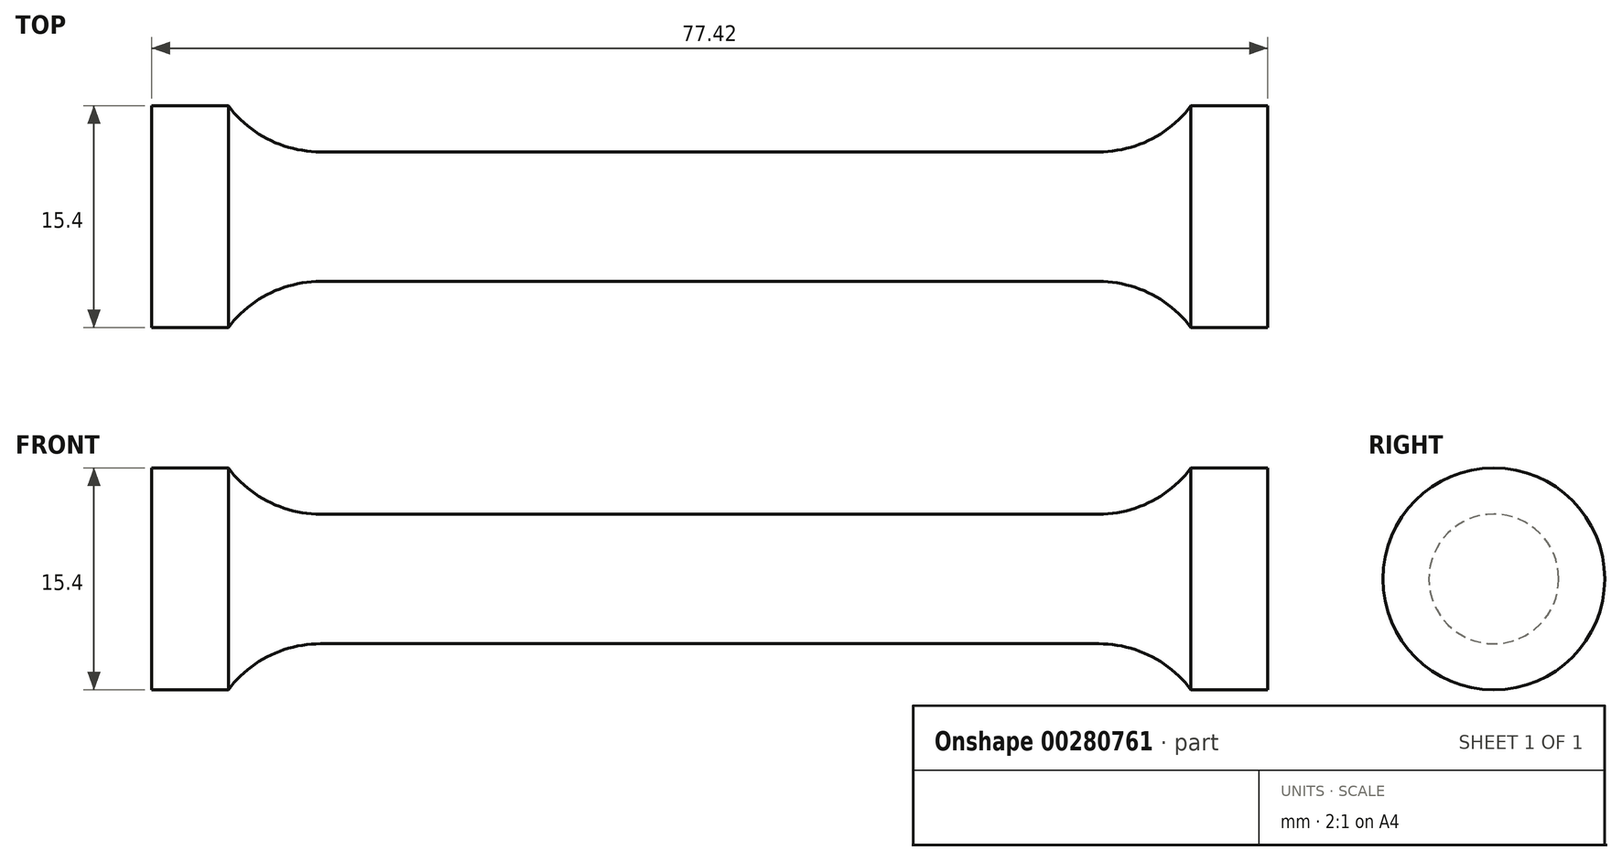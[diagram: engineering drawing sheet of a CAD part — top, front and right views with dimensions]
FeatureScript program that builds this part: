
annotation { "Feature Type Name" : "Feature", "Feature Type Description" : "" }
export const myFeature = defineFeature(function(context is Context, id is Id, definition is map)
    precondition{}
    {
        {
            var Q0;
            Q0=qCreatedBy(makeId("Front.planeOp"),FACE);
            var sketch = newSketch(context, id + "F0", { "sketchPlane" : qUnion([Q0])});
            skLineSegment(sketch, "E0", {"start": v(0, 4.5) * mm, "end": v(27, 4.5) * mm});
            skArc(sketch, "E1", {"start": v(27, 4.5) * mm, "mid": v(30.58, 5.34) * mm, "end": v(33.4, 7.7) * mm});
            skLineSegment(sketch, "E2", {"start": v(33.4, 7.7) * mm, "end": v(38.7, 7.7) * mm});
            skLineSegment(sketch, "E3", {"start": v(38.7, 7.7) * mm, "end": v(38.7, 0) * mm});
            skLineSegment(sketch, "E4.MirrorCS", {"start": v(0, 4.5) * mm, "end": v(-27, 4.5) * mm});
            skLineSegment(sketch, "E5.MirrorCS", {"start": v(-38.7, 7.7) * mm, "end": v(-38.7, 0) * mm});
            skLineSegment(sketch, "E6.MirrorCS", {"start": v(-33.4, 7.7) * mm, "end": v(-38.7, 7.7) * mm});
            skArc(sketch, "E7.MirrorCS", {"start": v(-27, 4.5) * mm, "mid": v(-30.58, 5.34) * mm, "end": v(-33.4, 7.7) * mm});
            skLineSegment(sketch, "E8", {"start": v(-38.7, 0) * mm, "end": v(38.7, 0) * mm});
            skSolve(sketch);
        }
        {
            var Q0;
            Q0=makeQuery(id+"F0.imprint","IMPRINT",FACE,{"disambiguationData":[TD([[makeQuery(id+"F0.imprint","IMPRINT",EDGE,{"derivedFrom":sQuery(id+"F0.wireOp",EDGE,"E0")}),-1.0]])]});
            var Q1;
            Q1=sQuery(id+"F0.wireOp",EDGE,"E8");
            revolve(context, id + "F1", {"entities" : qUnion([Q0]), "axis" : qUnion([Q1]), "revolveType" : RevolveType.FULL});
        }
    });
